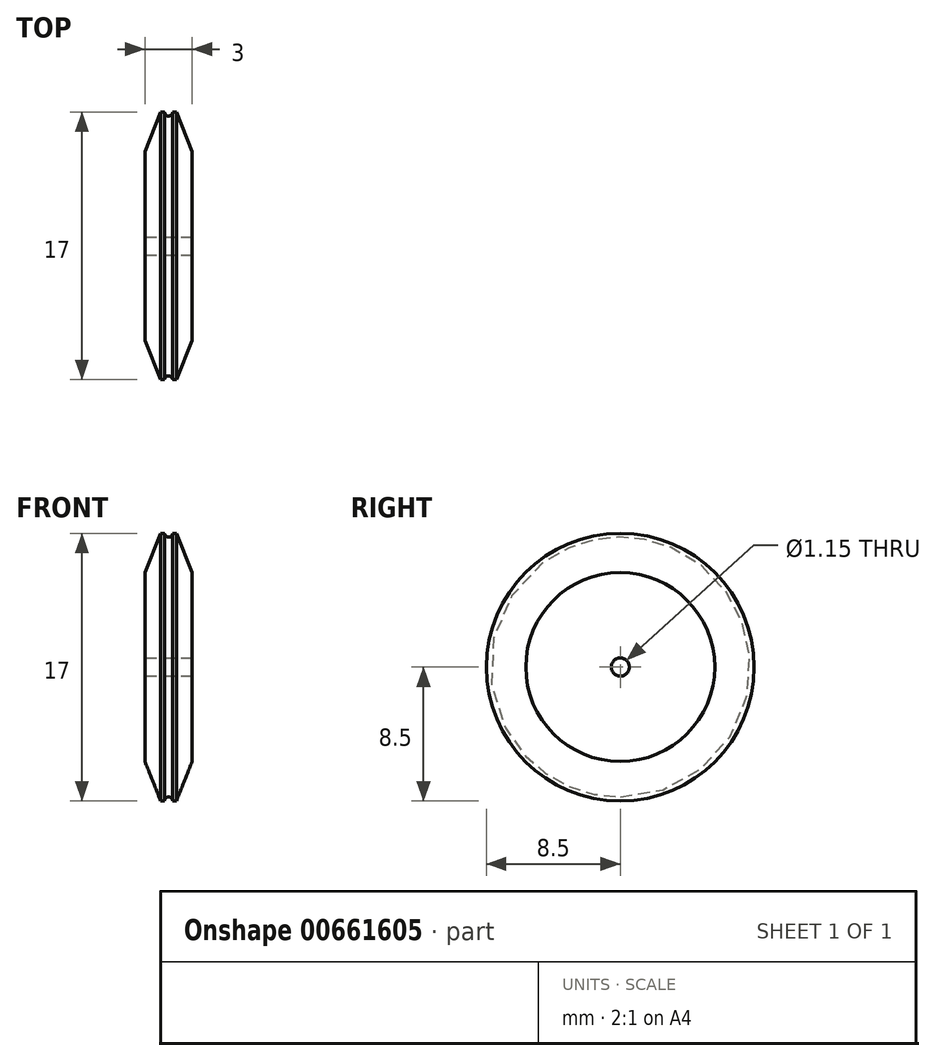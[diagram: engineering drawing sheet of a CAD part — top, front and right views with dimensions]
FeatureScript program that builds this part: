
annotation { "Feature Type Name" : "Feature", "Feature Type Description" : "" }
export const myFeature = defineFeature(function(context is Context, id is Id, definition is map)
    precondition{}
    {
        {
            var Q0;
            Q0=qCreatedBy(makeId("Front.planeOp"),FACE);
            var sketch = newSketch(context, id + "F0", { "sketchPlane" : qUnion([Q0])});
            skLineSegment(sketch, "E0.bottom", {"start": v(1.5, 0) * mm, "end": v(-1.5, 0) * mm});
            skLineSegment(sketch, "E0.left", {"start": v(1.5, 0) * mm, "end": v(1.5, 6) * mm});
            skLineSegment(sketch, "E0.right", {"start": v(-1.5, 0) * mm, "end": v(-1.5, 6) * mm});
            skLineSegment(sketch, "E1", {"start": v(-1.5, 6) * mm, "end": v(-0.5, 8.5) * mm});
            skLineSegment(sketch, "E2", {"start": v(-0.5, 8.5) * mm, "end": v(0.5, 8.5) * mm});
            skLineSegment(sketch, "E3", {"start": v(0.5, 8.5) * mm, "end": v(1.5, 6) * mm});
            skLineSegment(sketch, "E4", {"start": v(0, 8.5) * mm, "end": v(0, 0) * mm, "construction": true});
            skSolve(sketch);
        }
        {
            var Q0;
            Q0=makeQuery(id+"F0.imprint","IMPRINT",FACE,{"disambiguationData":[TD([[makeQuery(id+"F0.imprint","IMPRINT",EDGE,{"derivedFrom":sQuery(id+"F0.wireOp",EDGE,"E0.bottom")}),-1.0]])]});
            var Q1;
            Q1=sQuery(id+"F0.wireOp",EDGE,"E0.bottom");
            revolve(context, id + "F1", {"entities" : qUnion([Q0]), "axis" : qUnion([Q1]), "revolveType" : RevolveType.FULL});
        }
        {
            var Q0;
            Q0=qCreatedBy(makeId("Front.planeOp"),FACE);
            var sketch = newSketch(context, id + "F2", { "sketchPlane" : qUnion([Q0])});
            skCircle(sketch, "E5", {"center": v(0, 8.5) * mm, "radius": 0.25 * mm});
            skLineSegment(sketch, "E6", {"start": v(0, 0) * mm, "end": v(1.48, 0) * mm, "construction": true});
            skSolve(sketch);
        }
        {
            var Q0;
            Q0 = qSketchRegion(id + "F2", true);
            var Q1;
            Q1=sQuery(id+"F2.wireOp",EDGE,"E6");
            revolve(context, id + "F3", {"operationType" : NewBodyOperationType.REMOVE, "entities" : qUnion([Q0]), "axis" : qUnion([Q1]), "revolveType" : RevolveType.FULL, "oppositeDirection" : true});
        }
        {
            var Q0;
            Q0=makeQuery(id+"F1.opRevolve","SWEPT_FACE",FACE,{"disambiguationData":[OSD([sQuery(id+"F0.wireOp",EDGE,"E0.left")])]});
            var sketch = newSketch(context, id + "F4", { "sketchPlane" : qUnion([Q0])});
            skCircle(sketch, "E7", {"center": v(0, 0) * mm, "radius": 0.58 * mm});
            skSolve(sketch);
        }
        {
            var Q0;
            Q0 = qSketchRegion(id + "F4", true);
            extrude(context, id + "F5", {"entities" : qUnion([Q0]), "operationType" : NewBodyOperationType.REMOVE, "endBound" : BoundingType.UP_TO_NEXT, "oppositeDirection" : true, "depth" : 25 * mm, "offsetDistance" : 25 * mm});
        }
    });
